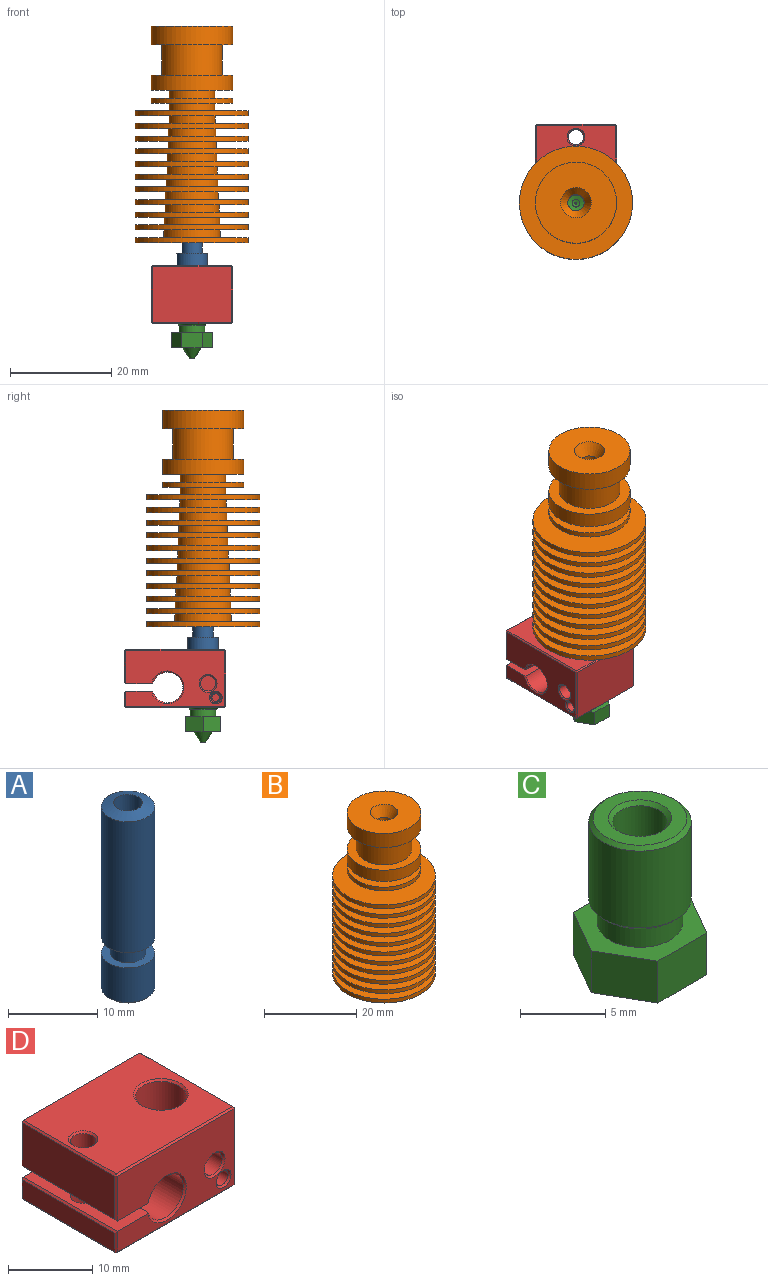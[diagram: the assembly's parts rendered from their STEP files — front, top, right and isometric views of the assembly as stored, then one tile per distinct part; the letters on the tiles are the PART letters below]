
ASSEMBLY  parts=4 mates=3
PART A: 9 faces, bbox 6x6x25.6 mm
  f0: cone r=1.6mm half-angle=70deg, axis (0,0,-1), area 21.5mm2, adj f1,f8
  f1: cylinder r=1.6mm len=25.61mm, axis (0,0,1), area 257.5mm2, adj f0,f2
  f2: plane 5.5x5.5mm, normal (0,0,-1), area 15.7mm2, adj f1,f3
  f3: cone r=2.75mm half-angle=45deg, axis (0,0,1), area 6.4mm2, adj f2,f4
  f4: cylinder r=3mm len=6mm, axis (0,0,1), area 89.5mm2, adj f3,f5
  f5: plane 6x6mm, normal (0,0,1), area 15.7mm2, adj f4,f6
  f6: cylinder r=2mm len=4mm, axis (0,0,1), area 26.4mm2, adj f5,f7
  f7: plane 6x6mm, normal (0,0,-1), area 15.7mm2, adj f6,f8
  f8: cylinder r=3mm len=18mm, axis (0,0,1), area 339.3mm2, adj f0,f7
PART B: 59 faces, bbox 22.3x22.3x42.7 mm
  f0: cone r=1.6mm half-angle=70deg, axis (0,0,-1), area 21.5mm2, adj f1,f58
  f1: cylinder r=3mm len=18mm, axis (0,0,1), area 339.3mm2, adj f0,f2
  f2: plane 22.3x22.3mm, normal (0,0,-1), area 362.3mm2, adj f1,f3
  f3: cylinder r=11.15mm len=22.3mm, axis (0,0,1), area 70.1mm2, adj f2,f4
  f4: plane 22.3x22.3mm, normal (0,0,1), area 293.6mm2, adj f3,f5
  f5: cylinder r=5.56mm len=11.11mm, axis (0,0,1), area 52.4mm2, adj f4,f6
  f6: plane 22.3x22.3mm, normal (0,0,-1), area 293.6mm2, adj f5,f7
  f7: cylinder r=11.15mm len=22.3mm, axis (0,0,1), area 70.1mm2, adj f6,f8
  f8: plane 22.3x22.3mm, normal (0,0,1), area 297.4mm2, adj f7,f9
  f9: cylinder r=5.45mm len=10.89mm, axis (0,0,1), area 51.3mm2, adj f8,f10
  f10: plane 22.3x22.3mm, normal (0,0,-1), area 297.4mm2, adj f9,f11
  f11: cylinder r=11.15mm len=22.3mm, axis (0,0,1), area 70.1mm2, adj f10,f12
  f12: plane 22.3x22.3mm, normal (0,0,1), area 301.1mm2, adj f11,f13
  f13: cylinder r=5.34mm len=10.68mm, axis (0,0,1), area 50.3mm2, adj f12,f14
  f14: plane 22.3x22.3mm, normal (0,0,-1), area 301.1mm2, adj f13,f15
  f15: cylinder r=11.15mm len=22.3mm, axis (0,0,1), area 70.1mm2, adj f14,f16
  f16: plane 22.3x22.3mm, normal (0,0,1), area 304.7mm2, adj f15,f17
  f17: cylinder r=5.23mm len=10.46mm, axis (0,0,1), area 49.3mm2, adj f16,f18
  f18: plane 22.3x22.3mm, normal (0,0,-1), area 304.7mm2, adj f17,f19
  f19: cylinder r=11.15mm len=22.3mm, axis (0,0,1), area 70.1mm2, adj f18,f20
  f20: plane 22.3x22.3mm, normal (0,0,1), area 308.2mm2, adj f19,f21
  f21: cylinder r=5.12mm len=10.24mm, axis (0,0,1), area 48.3mm2, adj f20,f22
  f22: plane 22.3x22.3mm, normal (0,0,-1), area 308.2mm2, adj f21,f23
  f23: cylinder r=11.15mm len=22.3mm, axis (0,0,1), area 70.1mm2, adj f22,f24
  f24: plane 22.3x22.3mm, normal (0,0,1), area 311.7mm2, adj f23,f25
  f25: cylinder r=5.01mm len=10.02mm, axis (0,0,1), area 47.2mm2, adj f24,f26
  f26: plane 22.3x22.3mm, normal (0,0,-1), area 311.7mm2, adj f25,f27
  f27: cylinder r=11.15mm len=22.3mm, axis (0,0,1), area 70.1mm2, adj f26,f28
  f28: plane 22.3x22.3mm, normal (0,0,1), area 315.1mm2, adj f27,f29
  f29: cylinder r=4.9mm len=9.8mm, axis (0,0,1), area 46.2mm2, adj f28,f30
  f30: plane 22.3x22.3mm, normal (0,0,-1), area 315.1mm2, adj f29,f31
  f31: cylinder r=11.15mm len=22.3mm, axis (0,0,1), area 70.1mm2, adj f30,f32
  f32: plane 22.3x22.3mm, normal (0,0,1), area 318.4mm2, adj f31,f33
  f33: cylinder r=4.79mm len=9.58mm, axis (0,0,1), area 45.2mm2, adj f32,f34
  f34: plane 22.3x22.3mm, normal (0,0,-1), area 318.4mm2, adj f33,f35
  f35: cylinder r=11.15mm len=22.3mm, axis (0,0,1), area 70.1mm2, adj f34,f36
  f36: plane 22.3x22.3mm, normal (0,0,1), area 321.7mm2, adj f35,f37
  f37: cylinder r=4.68mm len=9.37mm, axis (0,0,1), area 44.1mm2, adj f36,f38
  f38: plane 22.3x22.3mm, normal (0,0,-1), area 321.7mm2, adj f37,f39
  f39: cylinder r=11.15mm len=22.3mm, axis (0,0,1), area 70.1mm2, adj f38,f40
  f40: plane 22.3x22.3mm, normal (0,0,1), area 324.8mm2, adj f39,f41
  f41: cylinder r=4.57mm len=9.15mm, axis (0,0,1), area 43.1mm2, adj f40,f42
  f42: plane 22.3x22.3mm, normal (0,0,-1), area 324.8mm2, adj f41,f43
  f43: cylinder r=11.15mm len=22.3mm, axis (0,0,1), area 70.1mm2, adj f42,f44
  f44: plane 22.3x22.3mm, normal (0,0,1), area 327.9mm2, adj f43,f45
  f45: cylinder r=4.46mm len=8.93mm, axis (0,0,1), area 42.1mm2, adj f44,f46
  f46: plane 16x16mm, normal (0,0,-1), area 138.4mm2, adj f45,f47
  f47: cylinder r=8mm len=16mm, axis (0,0,1), area 50.3mm2, adj f46,f48
  f48: plane 16x16mm, normal (0,0,1), area 138.4mm2, adj f47,f49
  f49: cylinder r=4.46mm len=8.93mm, axis (0,0,1), area 42.1mm2, adj f48,f50
  f50: plane 16x16mm, normal (0,0,-1), area 138.4mm2, adj f49,f51
  f51: cylinder r=8mm len=16mm, axis (0,0,1), area 150.8mm2, adj f50,f52
  f52: plane 16x16mm, normal (0,0,1), area 88mm2, adj f51,f53
  f53: cylinder r=6mm len=12mm, axis (0,0,1), area 226.2mm2, adj f52,f54
  f54: plane 16x16mm, normal (0,0,-1), area 88mm2, adj f53,f55
  f55: cylinder r=8mm len=16mm, axis (0,0,1), area 186mm2, adj f54,f56
  f56: plane 16x16mm, normal (0,0,1), area 172.8mm2, adj f55,f57
  f57: cone r=3mm half-angle=30deg, axis (0,0,1), area 40.5mm2, adj f56,f58
  f58: cylinder r=1.6mm len=21.77mm, axis (0,0,1), area 218.8mm2, adj f0,f57
PART C: 22 faces, bbox 8.1x7x12.5 mm
  f0: cone r=2.75mm half-angle=45deg, axis (0,0,-1), area 6.4mm2, adj f1,f15
  f1: plane 5.5x5.5mm, normal (0,0,1), area 13mm2, adj f0,f2
  f2: cone r=1.6mm half-angle=45deg, axis (0,0,1), area 3.8mm2, adj f1,f3
  f3: cylinder r=1.6mm len=9.85mm, axis (0,0,1), area 99mm2, adj f2,f4
  f4: cone r=0.75mm half-angle=73.3deg, axis (0,0,1), area 6.6mm2, adj f3,f5
  f5: cylinder r=0.75mm len=1.5mm, axis (0,0,1), area 5.6mm2, adj f4,f6
  f6: cone r=0.2mm half-angle=73.3deg, axis (0,0,1), area 1.7mm2, adj f5,f7
  f7: cylinder r=0.2mm len=0.8mm, axis (0,0,1), area 1mm2, adj f6,f8
  f8: plane 1x1mm, normal (0,0,-1), area 0.7mm2, adj f7,f9
  f9: cone r=1.9mm half-angle=35deg, axis (0,0,1), area 18.4mm2, adj f8,f10
  f10: plane 8.08x7mm, normal (0,0,-1), area 31.1mm2, adj f9,f16,f17,f18,f19,f20,f21
  f11: plane 8.08x7mm, normal (0,0,1), area 22.8mm2, adj f12,f16,f17,f18,f19,f20,f21
  f12: cylinder r=2.5mm len=5mm, axis (0,0,1), area 23.6mm2, adj f11,f13
  f13: plane 5.5x5.5mm, normal (0,0,-1), area 4.1mm2, adj f12,f14
  f14: cone r=3mm half-angle=45deg, axis (0,0,1), area 6.4mm2, adj f13,f15
  f15: cylinder r=3mm len=6mm, axis (0,0,1), area 103.7mm2, adj f0,f14
  f16: plane 4.04x3mm, normal (0,-1,0), area 12.1mm2, adj f10,f11,f17,f19
  f17: plane 3.5x3mm, normal (0.87,-0.5,0), area 12.1mm2, adj f10,f11,f16,f18
  f18: plane 3.5x3mm, normal (0.87,0.5,0), area 12.1mm2, adj f10,f11,f17,f20
  f19: plane 3.5x3mm, normal (-0.87,-0.5,0), area 12.1mm2, adj f10,f11,f16,f21
  f20: plane 4.04x3mm, normal (0,1,0), area 12.1mm2, adj f10,f11,f18,f21
  f21: plane 3.5x3mm, normal (-0.87,0.5,0), area 12.1mm2, adj f10,f11,f19,f20
PART D: 55 faces, bbox 20x16x11.5 mm
  f0: plane 15.5x6.25mm, normal (-1,0,0), area 96.9mm2, adj f24,f27,f30,f31
  f1: plane 19.5x11mm, normal (0,-1,0), area 159.2mm2, adj f10,f11,f19,f20,f21,f27,f32,f39
  f2: cylinder r=1.5mm len=6.5mm, axis (0,0,1), area 61.3mm2, adj f10,f23
  f3: cylinder r=1.5mm len=3mm, axis (0,0,1), area 28.3mm2, adj f11,f54
  f4: plane 19.5x11mm, normal (0,1,0), area 171.2mm2, adj f25,f30,f34,f38,f41,f42,f45,f46
  f5: plane 15.5x2.75mm, normal (-1,0,0), area 42.6mm2, adj f45,f48,f51,f52
  f6: plane 15.5x11mm, normal (1,0,0), area 170.5mm2, adj f33,f34,f39,f40
  f7: cylinder r=3mm len=11mm, axis (0,0,1), area 207.3mm2, adj f22,f53
  f8: plane 19.5x15.5mm, normal (0,0,-1), area 259.4mm2, adj f40,f41,f47,f48,f53,f54
  f9: plane 19.5x15.5mm, normal (0,0,1), area 259.4mm2, adj f22,f23,f24,f25,f32,f33
  f10: plane 15.75x5.35mm, normal (0,0,-1), area 77.1mm2, adj f1,f2,f12,f19,f31,f38
  f11: plane 15.75x5.35mm, normal (0,0,1), area 77.1mm2, adj f1,f3,f12,f19,f46,f51
  f12: cylinder r=3mm len=15.5mm, axis (0,-1,0), area 268.7mm2, adj f10,f11,f19,f42
  f13: cylinder r=1.5mm len=3.25mm, axis (0,-1,0), area 30.6mm2, adj f14,f21
  f14: plane 3x3mm, normal (0,-1,0), area 7.1mm2, adj f13
  f15: cylinder r=1mm len=2mm, axis (0,-1,0), area 11mm2, adj f16,f20
  f16: plane 2x2mm, normal (0,-1,0), area 1.4mm2, adj f15,f18
  f17: plane 1.5x1.5mm, normal (0,-1,0), area 1.8mm2, adj f18
  f18: cylinder r=0.75mm len=2.5mm, axis (0,-1,0), area 11.8mm2, adj f16,f17
  f19: cone r=3mm half-angle=45deg, axis (0,-1,0), area 6.4mm2, adj f1,f10,f11,f12
  f20: cone r=1mm half-angle=45deg, axis (0,-1,0), area 2.5mm2, adj f1,f15
  f21: cone r=1.5mm half-angle=45deg, axis (0,-1,0), area 3.6mm2, adj f1,f13
  f22: cone r=3mm half-angle=45deg, axis (0,0,1), area 6.9mm2, adj f7,f9
  f23: cone r=1.5mm half-angle=45deg, axis (0,0,1), area 3.6mm2, adj f2,f9
  f24: plane 15.5x0.25mm, normal (-0.71,0,0.71), area 5.5mm2, adj f0,f9,f26,f28
  f25: plane 19.5x0.25mm, normal (0,0.71,0.71), area 6.9mm2, adj f4,f9,f26,f29
  f26: plane 0.25x0.25mm, normal (-0.58,0.58,0.58), area 0.1mm2, adj f24,f25,f30
  f27: plane 6.5x0.25mm, normal (-0.71,-0.71,0), area 2.3mm2, adj f0,f1,f28,f31
  f28: plane 0.25x0.25mm, normal (-0.58,-0.58,0.58), area 0.1mm2, adj f24,f27,f32
  f29: plane 0.25x0.25mm, normal (0.58,0.58,0.58), area 0.1mm2, adj f25,f33,f34
  f30: plane 6.25x0.25mm, normal (-0.71,0.71,0), area 2.2mm2, adj f0,f4,f26,f35
  f31: plane 15.75x0.25mm, normal (-0.71,0,-0.71), area 5.5mm2, adj f0,f10,f27,f35
  f32: plane 19.5x0.25mm, normal (0,-0.71,0.71), area 6.9mm2, adj f1,f9,f28,f36
  f33: plane 15.5x0.25mm, normal (0.71,0,0.71), area 5.5mm2, adj f6,f9,f29,f36
  f34: plane 11x0.25mm, normal (0.71,0.71,0), area 3.9mm2, adj f4,f6,f29,f37
  f35: plane 0.25x0.25mm, normal (-0.58,0.58,-0.58), area 0.1mm2, adj f30,f31,f38
  f36: plane 0.25x0.25mm, normal (0.58,-0.58,0.58), area 0.1mm2, adj f32,f33,f39
  f37: plane 0.25x0.25mm, normal (0.58,0.58,-0.58), area 0.1mm2, adj f34,f40,f41
  f38: plane 5.35x0.26mm, normal (0,0.71,-0.71), area 1.9mm2, adj f4,f10,f35,f42
  f39: plane 11x0.25mm, normal (0.71,-0.71,0), area 3.9mm2, adj f1,f6,f36,f43
  f40: plane 15.5x0.25mm, normal (0.71,0,-0.71), area 5.5mm2, adj f6,f8,f37,f43
  f41: plane 19.5x0.25mm, normal (0,0.71,-0.71), area 6.9mm2, adj f4,f8,f37,f44
  f42: cone r=3.25mm half-angle=45deg, axis (0,1,0), area 6.3mm2, adj f4,f12,f38,f46
  f43: plane 0.25x0.25mm, normal (0.58,-0.58,-0.58), area 0.1mm2, adj f39,f40,f47
  f44: plane 0.25x0.25mm, normal (-0.58,0.58,-0.58), area 0.1mm2, adj f41,f45,f48
  f45: plane 2.75x0.25mm, normal (-0.71,0.71,0), area 1mm2, adj f4,f5,f44,f49
  f46: plane 5.35x0.26mm, normal (0,0.71,0.71), area 1.9mm2, adj f4,f11,f42,f49
  f47: plane 19.5x0.25mm, normal (0,-0.71,-0.71), area 6.9mm2, adj f1,f8,f43,f50
  f48: plane 15.5x0.25mm, normal (-0.71,0,-0.71), area 5.5mm2, adj f5,f8,f44,f50
  f49: plane 0.25x0.25mm, normal (-0.58,0.58,0.58), area 0.1mm2, adj f45,f46,f51
  f50: plane 0.25x0.25mm, normal (-0.58,-0.58,-0.58), area 0.1mm2, adj f47,f48,f52
  f51: plane 15.75x0.25mm, normal (-0.71,0,0.71), area 5.5mm2, adj f5,f11,f49,f52
  f52: plane 3x0.25mm, normal (-0.71,-0.71,0), area 1mm2, adj f1,f5,f50,f51
  f53: cone r=3.25mm half-angle=45deg, axis (0,0,-1), area 6.9mm2, adj f7,f8
  f54: cone r=1.75mm half-angle=45deg, axis (0,0,-1), area 3.6mm2, adj f3,f8
PLACE A t=(-17.01,-6.26,-11.86)mm
PLACE B t=(-17.01,-6.26,-11.86)mm
PLACE C t=(-17.01,-6.26,-14.99)mm
PLACE D rot(axis=(0,0,-1),90deg) t=(-17.01,-6.26,-14.24)mm
MATE revolute A.f3 <-> B.f1  axis (0,0,1) through (-17.01,-6.26,-2.86)mm
MATE revolute D.f7 <-> C.f6  axis (0,0,-1) through (-17.01,-6.26,-27.84)mm
MATE revolute A.f3 <-> D.f22  axis (0,0,1) through (-17.01,-6.26,-16.34)mm
